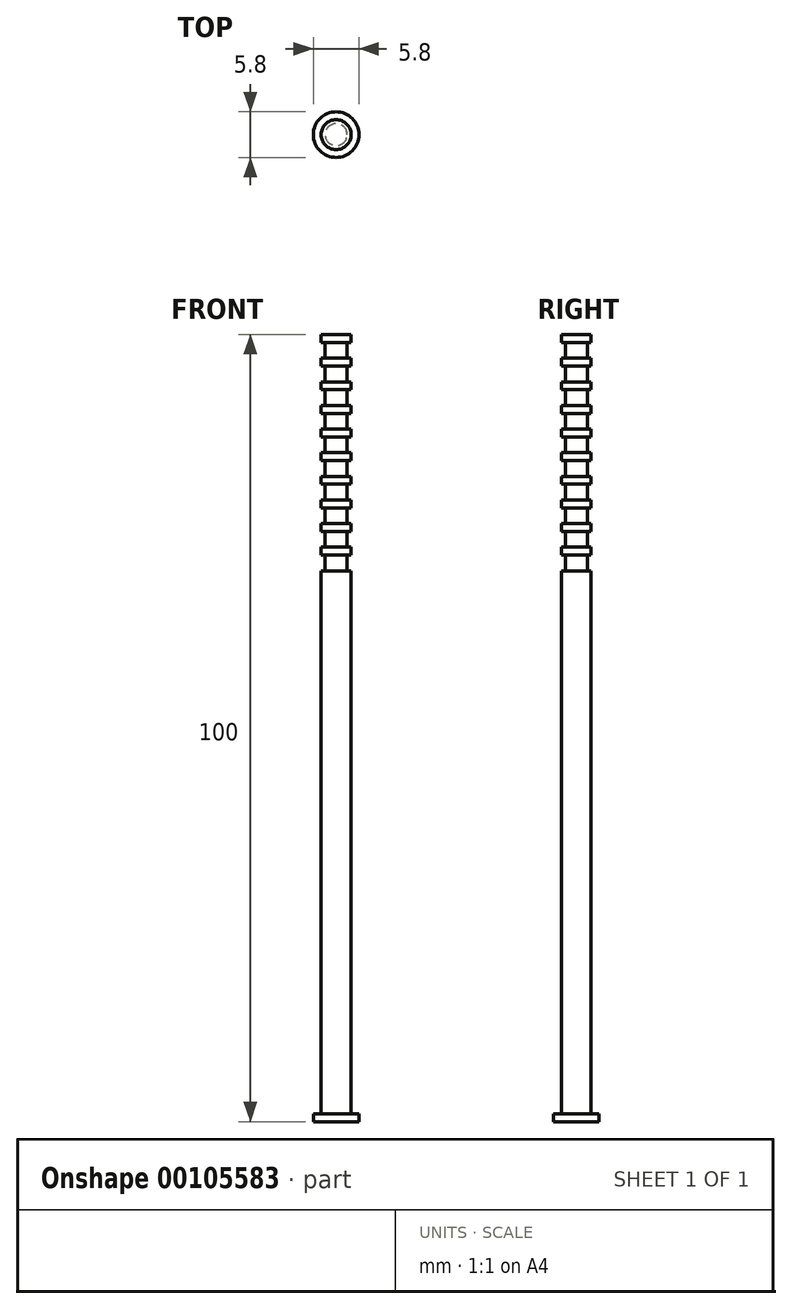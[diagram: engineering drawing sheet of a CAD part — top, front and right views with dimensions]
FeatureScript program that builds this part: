
annotation { "Feature Type Name" : "Feature", "Feature Type Description" : "" }
export const myFeature = defineFeature(function(context is Context, id is Id, definition is map)
    precondition{}
    {
        {
            var Q0;
            Q0=qCreatedBy(makeId("Front.planeOp"),FACE);
            var sketch = newSketch(context, id + "F0", { "sketchPlane" : qUnion([Q0])});
            skLineSegment(sketch, "E0.bottom", {"start": v(0, 50.12) * mm, "end": v(1.9, 50.12) * mm});
            skLineSegment(sketch, "E0.top", {"start": v(0, -49.88) * mm, "end": v(1.9, -49.88) * mm});
            skLineSegment(sketch, "E0.left", {"start": v(0, 50.12) * mm, "end": v(0, -49.88) * mm});
            skLineSegment(sketch, "E0.right", {"start": v(1.9, 50.12) * mm, "end": v(1.9, 49.12) * mm});
            skLineSegment(sketch, "E1.bottom", {"start": v(1.9, 49.12) * mm, "end": v(1.4, 49.12) * mm});
            skLineSegment(sketch, "E1.top", {"start": v(1.9, 47.12) * mm, "end": v(1.4, 47.12) * mm});
            skLineSegment(sketch, "E1.right", {"start": v(1.4, 49.12) * mm, "end": v(1.4, 47.12) * mm});
            skLineSegment(sketch, "E2.bottom", {"start": v(1.9, 46.12) * mm, "end": v(1.4, 46.12) * mm});
            skLineSegment(sketch, "E2.top", {"start": v(1.9, 44.12) * mm, "end": v(1.4, 44.12) * mm});
            skLineSegment(sketch, "E2.right", {"start": v(1.4, 46.12) * mm, "end": v(1.4, 44.12) * mm});
            skLineSegment(sketch, "E3.bottom", {"start": v(1.9, 43.12) * mm, "end": v(1.4, 43.12) * mm});
            skLineSegment(sketch, "E3.top", {"start": v(1.9, 41.12) * mm, "end": v(1.4, 41.12) * mm});
            skLineSegment(sketch, "E3.right", {"start": v(1.4, 43.12) * mm, "end": v(1.4, 41.12) * mm});
            skLineSegment(sketch, "E4.bottom", {"start": v(1.9, 40.12) * mm, "end": v(1.4, 40.12) * mm});
            skLineSegment(sketch, "E4.top", {"start": v(1.9, 38.12) * mm, "end": v(1.4, 38.12) * mm});
            skLineSegment(sketch, "E4.right", {"start": v(1.4, 40.12) * mm, "end": v(1.4, 38.12) * mm});
            skLineSegment(sketch, "E5.bottom", {"start": v(1.9, 37.12) * mm, "end": v(1.4, 37.12) * mm});
            skLineSegment(sketch, "E5.top", {"start": v(1.9, 35.12) * mm, "end": v(1.4, 35.12) * mm});
            skLineSegment(sketch, "E5.right", {"start": v(1.4, 37.12) * mm, "end": v(1.4, 35.12) * mm});
            skLineSegment(sketch, "E6.trimOffspring", {"start": v(1.9, 47.12) * mm, "end": v(1.9, 46.12) * mm});
            skLineSegment(sketch, "E7.trimOffspring", {"start": v(1.9, 44.12) * mm, "end": v(1.9, 43.12) * mm});
            skLineSegment(sketch, "E8.trimOffspring", {"start": v(1.9, 41.12) * mm, "end": v(1.9, 40.12) * mm});
            skLineSegment(sketch, "E9.trimOffspring", {"start": v(1.9, 38.12) * mm, "end": v(1.9, 37.12) * mm});
            skLineSegment(sketch, "E10.trimOffspring", {"start": v(1.9, -48.88) * mm, "end": v(1.9, -49.88) * mm});
            skLineSegment(sketch, "E11", {"start": v(1.9, 35.12) * mm, "end": v(1.9, 34.12) * mm});
            skLineSegment(sketch, "E12", {"start": v(1.9, 34.12) * mm, "end": v(1.9, 34.62) * mm});
            skLineSegment(sketch, "E13", {"start": v(1.9, 34.62) * mm, "end": v(0, 34.62) * mm, "construction": true});
            skLineSegment(sketch, "E14.MirrorCS", {"start": v(1.9, 31.12) * mm, "end": v(1.4, 31.12) * mm});
            skLineSegment(sketch, "E15.MirrorCS", {"start": v(1.9, 32.12) * mm, "end": v(1.4, 32.12) * mm});
            skLineSegment(sketch, "E16.MirrorCS", {"start": v(1.9, 25.12) * mm, "end": v(1.4, 25.12) * mm});
            skLineSegment(sketch, "E17.MirrorCS", {"start": v(1.9, 23.12) * mm, "end": v(1.4, 23.12) * mm});
            skLineSegment(sketch, "E18.MirrorCS", {"start": v(1.9, 22.12) * mm, "end": v(1.4, 22.12) * mm});
            skLineSegment(sketch, "E19.MirrorCS", {"start": v(1.9, 20.12) * mm, "end": v(1.4, 20.12) * mm});
            skLineSegment(sketch, "E20.MirrorCS", {"start": v(1.9, 28.12) * mm, "end": v(1.4, 28.12) * mm});
            skLineSegment(sketch, "E21.MirrorCS", {"start": v(1.9, 26.12) * mm, "end": v(1.4, 26.12) * mm});
            skLineSegment(sketch, "E22.MirrorCS", {"start": v(1.9, 29.12) * mm, "end": v(1.4, 29.12) * mm});
            skLineSegment(sketch, "E23.MirrorCS", {"start": v(1.9, 34.12) * mm, "end": v(1.4, 34.12) * mm});
            skLineSegment(sketch, "E24.MirrorCS", {"start": v(1.9, 34.12) * mm, "end": v(1.9, 35.12) * mm});
            skLineSegment(sketch, "E25.MirrorCS", {"start": v(1.4, 26.12) * mm, "end": v(1.4, 28.12) * mm});
            skLineSegment(sketch, "E26.MirrorCS", {"start": v(1.4, 32.12) * mm, "end": v(1.4, 34.12) * mm});
            skLineSegment(sketch, "E27.MirrorCS", {"start": v(1.9, 22.12) * mm, "end": v(1.9, 23.12) * mm});
            skLineSegment(sketch, "E28.MirrorCS", {"start": v(1.9, 28.12) * mm, "end": v(1.9, 29.12) * mm});
            skLineSegment(sketch, "E29.MirrorCS", {"start": v(1.4, 20.12) * mm, "end": v(1.4, 22.12) * mm});
            skLineSegment(sketch, "E30.MirrorCS", {"start": v(1.9, 19.12) * mm, "end": v(1.9, 20.12) * mm});
            skLineSegment(sketch, "E31.MirrorCS", {"start": v(1.4, 23.12) * mm, "end": v(1.4, 25.12) * mm});
            skLineSegment(sketch, "E32.MirrorCS", {"start": v(1.4, 29.12) * mm, "end": v(1.4, 31.12) * mm});
            skLineSegment(sketch, "E33.MirrorCS", {"start": v(1.9, 31.12) * mm, "end": v(1.9, 32.12) * mm});
            skLineSegment(sketch, "E34.MirrorCS", {"start": v(1.9, 25.12) * mm, "end": v(1.9, 26.12) * mm});
            skPoint(sketch, "E35.MirrorCS.start.orphan", {"position": v(0, 19.12) * mm});
            skLineSegment(sketch, "E36", {"start": v(1.9, 19.12) * mm, "end": v(1.9, -46.88) * mm});
            skLineSegment(sketch, "E37.bottom", {"start": v(1.9, -48.88) * mm, "end": v(1.4, -48.88) * mm});
            skLineSegment(sketch, "E37.top", {"start": v(1.9, -46.88) * mm, "end": v(1.4, -46.88) * mm});
            skLineSegment(sketch, "E37.right", {"start": v(1.4, -48.88) * mm, "end": v(1.4, -46.88) * mm});
            skLineSegment(sketch, "E38", {"start": v(1.9, -46.88) * mm, "end": v(1.9, -48.88) * mm});
            skLineSegment(sketch, "E39.bottom", {"start": v(1.9, -48.88) * mm, "end": v(2.9, -48.88) * mm});
            skLineSegment(sketch, "E39.top", {"start": v(1.9, -49.88) * mm, "end": v(2.9, -49.88) * mm});
            skLineSegment(sketch, "E39.right", {"start": v(2.9, -48.88) * mm, "end": v(2.9, -49.88) * mm});
            skSolve(sketch);
        }
        {
            var Q0;
            Q0 = qSketchRegion(id + "F0", true);
            var Q1;
            Q1=sQuery(id+"F0.wireOp",EDGE,"E0.left");
            revolve(context, id + "F1", {"entities" : qUnion([Q0]), "axis" : qUnion([Q1]), "revolveType" : RevolveType.FULL});
        }
    });
